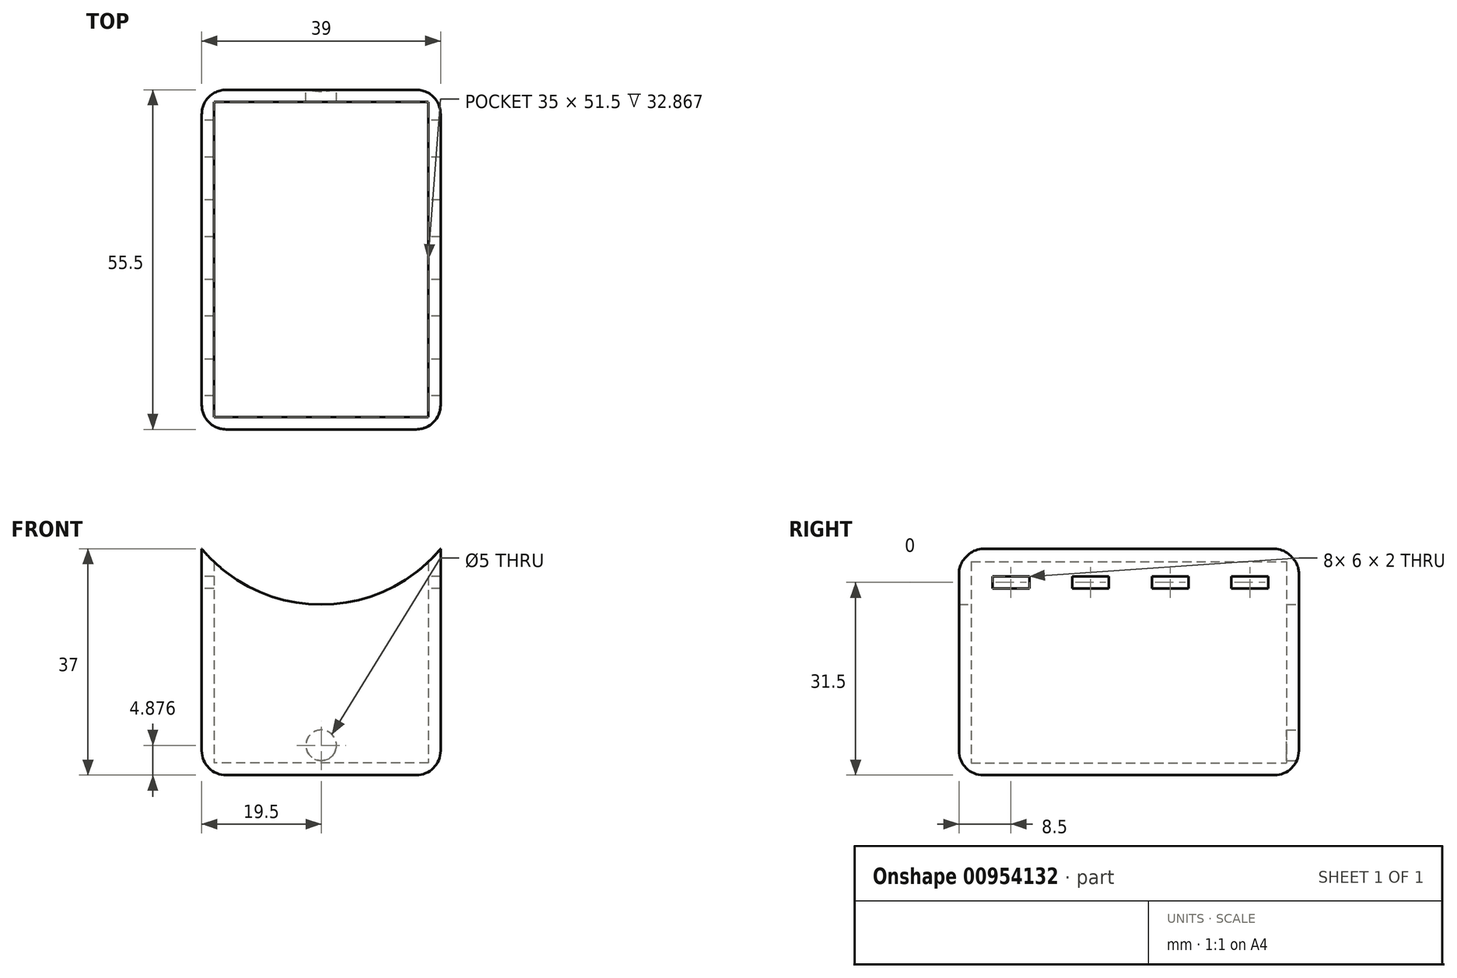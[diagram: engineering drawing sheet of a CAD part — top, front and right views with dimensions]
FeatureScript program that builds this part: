
annotation { "Feature Type Name" : "Feature", "Feature Type Description" : "" }
export const myFeature = defineFeature(function(context is Context, id is Id, definition is map)
    precondition{}
    {
        {
            var Q0;
            Q0=qCreatedBy(makeId("Top.planeOp"),FACE);
            var sketch = newSketch(context, id + "F0", { "sketchPlane" : qUnion([Q0])});
            skLineSegment(sketch, "E0.bottom", {"start": v(17.5, -25.75) * mm, "end": v(-17.5, -25.75) * mm});
            skLineSegment(sketch, "E0.top", {"start": v(17.5, 25.75) * mm, "end": v(-17.5, 25.75) * mm});
            skLineSegment(sketch, "E0.left", {"start": v(17.5, -25.75) * mm, "end": v(17.5, 25.75) * mm});
            skLineSegment(sketch, "E0.right", {"start": v(-17.5, -25.75) * mm, "end": v(-17.5, 25.75) * mm});
            skPoint(sketch, "E0.middle", {"position": v(0, 0) * mm});
            skLineSegment(sketch, "E1.0", {"start": v(19.5, 27.75) * mm, "end": v(-19.5, 27.75) * mm});
            skLineSegment(sketch, "E1.1", {"start": v(19.5, -27.75) * mm, "end": v(19.5, 27.75) * mm});
            skLineSegment(sketch, "E1.2", {"start": v(19.5, -27.75) * mm, "end": v(-19.5, -27.75) * mm});
            skLineSegment(sketch, "E1.3", {"start": v(-19.5, -27.75) * mm, "end": v(-19.5, 27.75) * mm});
            skSolve(sketch);
        }
        {
            var Q0;
            Q0=makeQuery(id+"F0.imprint","IMPRINT",FACE,{"disambiguationData":[TD([[makeQuery(id+"F0.imprint","IMPRINT",EDGE,{"derivedFrom":sQuery(id+"F0.wireOp",EDGE,"E0.bottom")}),1.0]])]});
            extrude(context, id + "F1", {"entities" : qUnion([Q0]), "depth" : 37 * mm, "offsetDistance" : 25 * mm});
        }
        {
            var Q0;
            Q0=makeQuery(id+"F1.opExtrude","SWEPT_FACE",FACE,{"disambiguationData":[OSD([sQuery(id+"F0.wireOp",EDGE,"E1.0")])]});
            var sketch = newSketch(context, id + "F2", { "sketchPlane" : qUnion([Q0])});
            skArc(sketch, "E2", {"start": v(-19.5, 37) * mm, "mid": v(0, 27.88) * mm, "end": v(19.5, 37) * mm});
            skLineSegment(sketch, "E3", {"start": v(-19.5, 37) * mm, "end": v(19.5, 37) * mm});
            skSolve(sketch);
        }
        {
            var Q0;
            Q0=makeQuery(id+"F2.imprint","IMPRINT",FACE,{"disambiguationData":[TD([[makeQuery(id+"F2.imprint","IMPRINT",EDGE,{"derivedFrom":sQuery(id+"F2.wireOp",EDGE,"E2")}),1.0]])]});
            extrude(context, id + "F3", {"entities" : qUnion([Q0]), "operationType" : NewBodyOperationType.REMOVE, "oppositeDirection" : true, "depth" : 56 * mm, "offsetDistance" : 25 * mm});
        }
        {
            var Q0;
            Q0=makeQuery(id+"F0.imprint","IMPRINT",FACE,{"disambiguationData":[TD([[makeQuery(id+"F0.imprint","IMPRINT",EDGE,{"derivedFrom":sQuery(id+"F0.wireOp",EDGE,"E0.bottom")}),-1.0]])]});
            extrude(context, id + "F4", {"entities" : qUnion([Q0]), "operationType" : NewBodyOperationType.ADD, "depth" : 2 * mm, "offsetDistance" : 25 * mm});
        }
        {
            var Q0;
            Q0=makeQuery(id+"F1.opExtrude","SWEPT_FACE",FACE,{"disambiguationData":[OSD([sQuery(id+"F0.wireOp",EDGE,"E1.0")])]});
            var sketch = newSketch(context, id + "F5", { "sketchPlane" : qUnion([Q0])});
            skCircle(sketch, "E4", {"center": v(0, 4.88) * mm, "radius": 2.5 * mm});
            skSolve(sketch);
        }
        {
            var Q0;
            Q0=makeQuery(id+"F5.imprint","IMPRINT",FACE,{"disambiguationData":[TD([[makeQuery(id+"F5.imprint","IMPRINT",EDGE,{"derivedFrom":sQuery(id+"F5.wireOp",EDGE,"E4")}),1.0]])]});
            extrude(context, id + "F6", {"entities" : qUnion([Q0]), "operationType" : NewBodyOperationType.REMOVE, "oppositeDirection" : true, "depth" : 3 * mm, "offsetDistance" : 25 * mm});
        }
        {
            var Q0;
            Q0=makeQuery(id+"F1.opExtrude","SWEPT_FACE",FACE,{"disambiguationData":[OSD([sQuery(id+"F0.wireOp",EDGE,"E1.3")])]});
            var sketch = newSketch(context, id + "F7", { "sketchPlane" : qUnion([Q0])});
            skLineSegment(sketch, "E5.bottom", {"start": v(-22.75, 32.5) * mm, "end": v(-16.75, 32.5) * mm});
            skLineSegment(sketch, "E5.top", {"start": v(-22.75, 30.5) * mm, "end": v(-16.75, 30.5) * mm});
            skLineSegment(sketch, "E5.left", {"start": v(-22.75, 32.5) * mm, "end": v(-22.75, 30.5) * mm});
            skLineSegment(sketch, "E5.right", {"start": v(-16.75, 32.5) * mm, "end": v(-16.75, 30.5) * mm});
            skLineSegment(sketch, "E6.1.0.0", {"start": v(-9.75, 32.5) * mm, "end": v(-3.75, 32.5) * mm});
            skLineSegment(sketch, "E6.1.0.1", {"start": v(-9.75, 32.5) * mm, "end": v(-9.75, 30.5) * mm});
            skLineSegment(sketch, "E6.1.0.2", {"start": v(-9.75, 30.5) * mm, "end": v(-3.75, 30.5) * mm});
            skLineSegment(sketch, "E6.1.0.3", {"start": v(-3.75, 32.5) * mm, "end": v(-3.75, 30.5) * mm});
            skLineSegment(sketch, "E6.2.0.0", {"start": v(3.25, 32.5) * mm, "end": v(9.25, 32.5) * mm});
            skLineSegment(sketch, "E6.2.0.1", {"start": v(3.25, 32.5) * mm, "end": v(3.25, 30.5) * mm});
            skLineSegment(sketch, "E6.2.0.2", {"start": v(3.25, 30.5) * mm, "end": v(9.25, 30.5) * mm});
            skLineSegment(sketch, "E6.2.0.3", {"start": v(9.25, 32.5) * mm, "end": v(9.25, 30.5) * mm});
            skLineSegment(sketch, "E6.direction1", {"start": v(-22.75, 32.5) * mm, "end": v(-9.75, 32.5) * mm, "construction": true});
            skLineSegment(sketch, "E7.0.3.0", {"start": v(16.25, 32.5) * mm, "end": v(22.25, 32.5) * mm});
            skLineSegment(sketch, "E7.3.3.0", {"start": v(16.25, 32.5) * mm, "end": v(16.25, 30.5) * mm});
            skLineSegment(sketch, "E7.6.3.0", {"start": v(16.25, 30.5) * mm, "end": v(22.25, 30.5) * mm});
            skLineSegment(sketch, "E7.9.3.0", {"start": v(22.25, 32.5) * mm, "end": v(22.25, 30.5) * mm});
            skSolve(sketch);
        }
        {
            var Q0;
            Q0=makeQuery(id+"F7.imprint","IMPRINT",FACE,{"disambiguationData":[TD([[makeQuery(id+"F7.imprint","IMPRINT",EDGE,{"derivedFrom":sQuery(id+"F7.wireOp",EDGE,"E5.bottom")}),-1.0]])]});
            var Q1;
            Q1=makeQuery(id+"F7.imprint","IMPRINT",FACE,{"disambiguationData":[TD([[makeQuery(id+"F7.imprint","IMPRINT",EDGE,{"derivedFrom":sQuery(id+"F7.wireOp",EDGE,"E6.1.0.0")}),-1.0]])]});
            var Q2;
            Q2=makeQuery(id+"F7.imprint","IMPRINT",FACE,{"disambiguationData":[TD([[makeQuery(id+"F7.imprint","IMPRINT",EDGE,{"derivedFrom":sQuery(id+"F7.wireOp",EDGE,"E6.2.0.0")}),-1.0]])]});
            var Q3;
            Q3=makeQuery(id+"F7.imprint","IMPRINT",FACE,{"disambiguationData":[TD([[makeQuery(id+"F7.imprint","IMPRINT",EDGE,{"derivedFrom":sQuery(id+"F7.wireOp",EDGE,"E7.0.3.0")}),-1.0]])]});
            extrude(context, id + "F8", {"entities" : qUnion([Q0, Q1, Q2, Q3]), "operationType" : NewBodyOperationType.REMOVE, "oppositeDirection" : true, "depth" : 40 * mm, "offsetDistance" : 25 * mm});
        }
        {
            var Q0;
            Q0=makeQuery(id+"F1.opExtrude","CAP_EDGE",EDGE,{"disambiguationData":[OSD([sQuery(id+"F0.wireOp",EDGE,"E1.3")])],"isStart":true});
            var Q1;
            Q1=makeQuery(id+"F1.opExtrude","CAP_EDGE",EDGE,{"disambiguationData":[OSD([sQuery(id+"F0.wireOp",EDGE,"E1.0")])],"isStart":true});
            var Q2;
            Q2=makeQuery(id+"F1.opExtrude","CAP_EDGE",EDGE,{"disambiguationData":[OSD([sQuery(id+"F0.wireOp",EDGE,"E1.1")])],"isStart":true});
            var Q3;
            Q3=makeQuery(id+"F1.opExtrude","CAP_EDGE",EDGE,{"disambiguationData":[OSD([sQuery(id+"F0.wireOp",EDGE,"E1.2")])],"isStart":true});
            var Q4;
            Q4=makeQuery(id+"F1.opExtrude","SWEPT_EDGE",EDGE,{"disambiguationData":[OSD([sQuery(id+"F0.wireOp",EDGE,"E1.2"),sQuery(id+"F0.wireOp",EDGE,"E1.3")])]});
            var Q5;
            Q5=makeQuery(id+"F1.opExtrude","SWEPT_EDGE",EDGE,{"disambiguationData":[OSD([sQuery(id+"F0.wireOp",EDGE,"E1.1"),sQuery(id+"F0.wireOp",EDGE,"E1.2")])]});
            var Q6;
            Q6=makeQuery(id+"F1.opExtrude","SWEPT_EDGE",EDGE,{"disambiguationData":[OSD([sQuery(id+"F0.wireOp",EDGE,"E1.0"),sQuery(id+"F0.wireOp",EDGE,"E1.1")])]});
            var Q7;
            Q7=makeQuery(id+"F1.opExtrude","SWEPT_EDGE",EDGE,{"disambiguationData":[OSD([sQuery(id+"F0.wireOp",EDGE,"E1.0"),sQuery(id+"F0.wireOp",EDGE,"E1.3")])]});
            fillet(context, id + "F9", {"entities" : qUnion([Q0, Q1, Q2, Q3, Q4, Q5, Q6, Q7]), "radius" : 4 * mm, "tangentPropagation" : true, "allowEdgeOverflow" : false});
        }
    });
